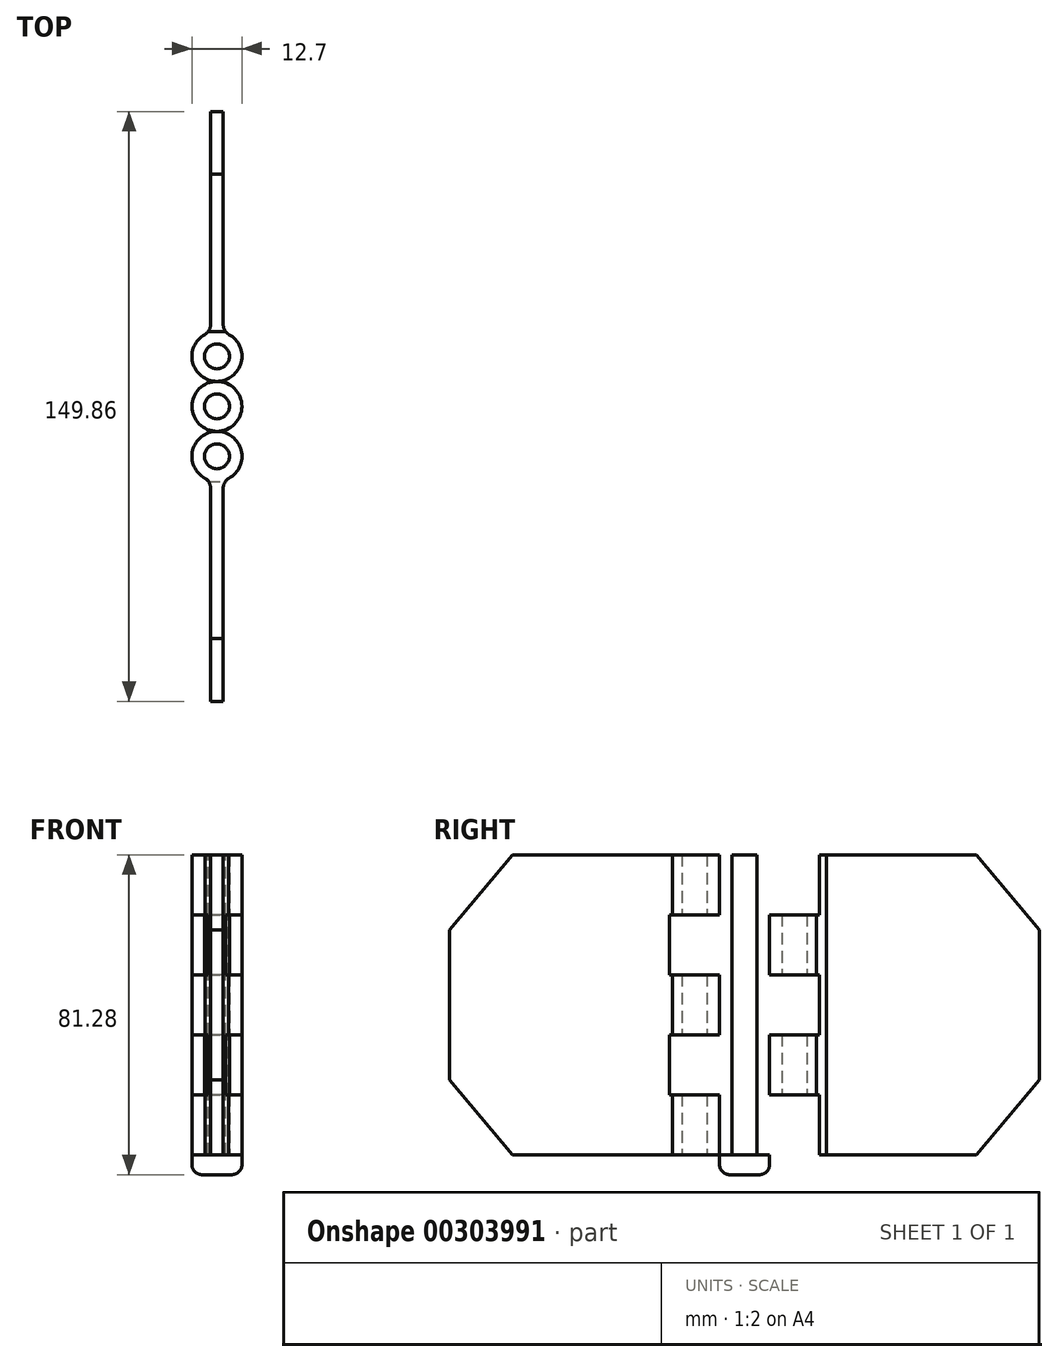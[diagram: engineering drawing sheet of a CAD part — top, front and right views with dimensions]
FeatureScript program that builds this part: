
annotation { "Feature Type Name" : "Feature", "Feature Type Description" : "" }
export const myFeature = defineFeature(function(context is Context, id is Id, definition is map)
    precondition{}
    {
        {
            var Q0;
            Q0=qCreatedBy(makeId("Right.planeOp"),FACE);
            var sketch = newSketch(context, id + "F0", { "sketchPlane" : qUnion([Q0])});
            skLineSegment(sketch, "E0.top", {"start": v(0, 76.2) * mm, "end": v(-39.9, 76.2) * mm});
            skLineSegment(sketch, "E0.left", {"start": v(0, 0) * mm, "end": v(0, 76.2) * mm});
            skLineSegment(sketch, "E1", {"start": v(-39.9, 76.2) * mm, "end": v(-55.88, 57.15) * mm});
            skLineSegment(sketch, "E2", {"start": v(-55.88, 19.05) * mm, "end": v(-39.9, 0) * mm});
            skLineSegment(sketch, "E3", {"start": v(-55.88, 57.15) * mm, "end": v(-55.88, 19.05) * mm});
            skLineSegment(sketch, "E4", {"start": v(-39.9, 0) * mm, "end": v(0, 0) * mm});
            skSolve(sketch);
        }
        {
            var Q0;
            Q0 = qSketchRegion(id + "F0", true);
            extrude(context, id + "F1", {"entities" : qUnion([Q0]), "depth" : 3.17 * mm});
        }
        {
            var Q0;
            Q0=makeQuery(id+"F1.opExtrude","SWEPT_FACE",FACE,{"disambiguationData":[OSD([sQuery(id+"F0.wireOp",EDGE,"E0.top")])]});
            var sketch = newSketch(context, id + "F2", { "sketchPlane" : qUnion([Q0])});
            skPoint(sketch, "E5", {"position": v(1.59, 6.35) * mm});
            skArc(sketch, "E6", {"start": v(4.6, 0.76) * mm, "mid": v(1.59, 12.7) * mm, "end": v(-1.43, 0.76) * mm});
            skArc(sketch, "E7", {"start": v(4.6, 0.76) * mm, "mid": v(3.56, -0.34) * mm, "end": v(3.18, -1.82) * mm});
            skArc(sketch, "E8", {"start": v(0, -1.82) * mm, "mid": v(-0.38, -0.34) * mm, "end": v(-1.43, 0.76) * mm});
            skLineSegment(sketch, "E9", {"start": v(0, -1.82) * mm, "end": v(0, 0) * mm});
            skLineSegment(sketch, "E10", {"start": v(0, 0) * mm, "end": v(3.18, 0) * mm});
            skLineSegment(sketch, "E11", {"start": v(3.18, 0) * mm, "end": v(3.18, -1.82) * mm});
            skPoint(sketch, "E12", {"position": v(1.59, 0) * mm});
            skSolve(sketch);
        }
        {
            var Q0;
            Q0 = qSketchRegion(id + "F2", true);
            var Q1;
            Q1=sQuery(id+"F2.wireOp",EDGE,"E6");
            extrude(context, id + "F3", {"entities" : qUnion([Q0]), "operationType" : NewBodyOperationType.ADD, "surfaceEntities" : qUnion([Q1]), "oppositeDirection" : true, "depth" : 76.2 * mm});
        }
        {
            var Q0;
            Q0=makeQuery(id+"F3.opExtrude","CAP_FACE",FACE,{"disambiguationData":[OSD([sQuery(id+"F2.wireOp",EDGE,"E6")])],"isStart":true});
            var sketch = newSketch(context, id + "F4", { "sketchPlane" : qUnion([Q0])});
            skPoint(sketch, "E13", {"position": v(1.59, 6.35) * mm});
            skCircle(sketch, "E14", {"center": v(1.59, 6.35) * mm, "radius": 3.18 * mm});
            skSolve(sketch);
        }
        {
            var Q0;
            Q0=sQuery(id+"F4.wireOp",VERTEX,"E13");
            var Q1;
            Q1=makeQuery(id+"F3.opExtrude","SWEPT_BODY",BODY,{"disambiguationData":[OSD([sQuery(id+"F2.wireOp",EDGE,"E6")])]});
            var Q2;
            Q2=makeQuery(id+"F1.opExtrude","SWEPT_BODY",BODY,{"disambiguationData":[OSD([sQuery(id+"F0.wireOp",EDGE,"E0.top"),sQuery(id+"F0.wireOp",EDGE,"E0.left"),sQuery(id+"F0.wireOp",EDGE,"E1"),sQuery(id+"F0.wireOp",EDGE,"E2"),sQuery(id+"F0.wireOp",EDGE,"E3"),sQuery(id+"F0.wireOp",EDGE,"E4")])]});
            hole(context, id + "F5", {"style" : HoleStyle.SIMPLE, "endStyle" : HoleEndStyle.THROUGH, "holeDiameter" : 6.35 * mm, "tappedDepth" : 12.7 * mm, "tapClearance" : 3, "locations" : qUnion([Q0]), "scope" : qUnion([Q1, Q2])});
        }
        {
            var Q0;
            Q0=qCreatedBy(makeId("Right.planeOp"),FACE);
            cPlane(context, id + "F6", {"entities" : qUnion([Q0]), "cplaneType" : CPlaneType.OFFSET, "offset" : 12.7 * mm, "width" : 152.4 * mm, "height" : 152.4 * mm});
        }
        {
            var Q0;
            Q0=qCreatedBy(id+"F6.planeOp",FACE);
            var sketch = newSketch(context, id + "F7", { "sketchPlane" : qUnion([Q0])});
            skLineSegment(sketch, "E15.bottom", {"start": v(12.7, 15.24) * mm, "end": v(0, 15.24) * mm});
            skLineSegment(sketch, "E15.top", {"start": v(12.7, 30.48) * mm, "end": v(0, 30.48) * mm});
            skLineSegment(sketch, "E15.left", {"start": v(12.7, 15.24) * mm, "end": v(12.7, 30.48) * mm});
            skLineSegment(sketch, "E15.right", {"start": v(0, 15.24) * mm, "end": v(0, 30.48) * mm});
            skLineSegment(sketch, "E16.bottom", {"start": v(12.7, 45.72) * mm, "end": v(0, 45.72) * mm});
            skLineSegment(sketch, "E16.top", {"start": v(12.7, 60.96) * mm, "end": v(0, 60.96) * mm});
            skLineSegment(sketch, "E16.left", {"start": v(12.7, 45.72) * mm, "end": v(12.7, 60.96) * mm});
            skLineSegment(sketch, "E16.right", {"start": v(0, 45.72) * mm, "end": v(0, 60.96) * mm});
            skSolve(sketch);
        }
        {
            var Q0;
            Q0 = qSketchRegion(id + "F7", true);
            extrude(context, id + "F8", {"entities" : qUnion([Q0]), "operationType" : NewBodyOperationType.REMOVE, "oppositeDirection" : true, "depth" : 19.05 * mm});
        }
        {
            var Q0;
            Q0=qCreatedBy(makeId("Right.planeOp"),FACE);
            var sketch = newSketch(context, id + "F9", { "sketchPlane" : qUnion([Q0])});
            skLineSegment(sketch, "E17.top", {"start": v(78, 76.2) * mm, "end": v(38.1, 76.2) * mm});
            skLineSegment(sketch, "E17.left", {"start": v(38.1, 0) * mm, "end": v(38.1, 76.2) * mm});
            skLineSegment(sketch, "E18", {"start": v(93.98, 57.15) * mm, "end": v(93.98, 19.05) * mm});
            skLineSegment(sketch, "E19", {"start": v(38.1, 0) * mm, "end": v(78, 0) * mm});
            skLineSegment(sketch, "E20", {"start": v(78, 76.2) * mm, "end": v(93.98, 57.15) * mm});
            skLineSegment(sketch, "E21", {"start": v(93.98, 19.05) * mm, "end": v(78, 0) * mm});
            skSolve(sketch);
        }
        {
            var Q0;
            Q0 = qSketchRegion(id + "F9", true);
            extrude(context, id + "F10", {"entities" : qUnion([Q0]), "depth" : 3.17 * mm});
        }
        {
            var Q0;
            Q0=makeQuery(id+"F10.opExtrude","SWEPT_FACE",FACE,{"disambiguationData":[OSD([sQuery(id+"F9.wireOp",EDGE,"E17.top")])]});
            var sketch = newSketch(context, id + "F11", { "sketchPlane" : qUnion([Q0])});
            skPoint(sketch, "E22", {"position": v(1.59, 38.1) * mm});
            skPoint(sketch, "E23", {"position": v(1.59, 31.75) * mm});
            skArc(sketch, "E24", {"start": v(-1.43, 37.34) * mm, "mid": v(1.59, 25.4) * mm, "end": v(4.6, 37.34) * mm});
            skArc(sketch, "E25", {"start": v(-1.43, 37.34) * mm, "mid": v(-0.4, 38.43) * mm, "end": v(0, 39.88) * mm});
            skArc(sketch, "E26", {"start": v(3.18, 39.88) * mm, "mid": v(3.57, 38.43) * mm, "end": v(4.6, 37.34) * mm});
            skLineSegment(sketch, "E27", {"start": v(0, 39.88) * mm, "end": v(0, 38.1) * mm});
            skLineSegment(sketch, "E28", {"start": v(0, 38.1) * mm, "end": v(3.18, 38.1) * mm});
            skLineSegment(sketch, "E29", {"start": v(3.18, 38.1) * mm, "end": v(3.18, 39.88) * mm});
            skSolve(sketch);
        }
        {
            var Q0;
            Q0 = qSketchRegion(id + "F11", true);
            extrude(context, id + "F12", {"entities" : qUnion([Q0]), "operationType" : NewBodyOperationType.ADD, "oppositeDirection" : true, "depth" : 76.2 * mm});
        }
        {
            var Q0;
            Q0=makeQuery(id+"F12.boolean.opBoolean","MERGE",FACE,{"derivedFrom":[makeQuery(id+"F10.opExtrude","SWEPT_FACE",FACE,{"disambiguationData":[OSD([sQuery(id+"F9.wireOp",EDGE,"E17.top")])]}),makeQuery(id+"F12.opExtrude","CAP_FACE",FACE,{"disambiguationData":[OSD([sQuery(id+"F11.wireOp",EDGE,"E24"),sQuery(id+"F11.wireOp",EDGE,"E25"),sQuery(id+"F11.wireOp",EDGE,"E26"),sQuery(id+"F11.wireOp",EDGE,"E27"),sQuery(id+"F11.wireOp",EDGE,"E28"),sQuery(id+"F11.wireOp",EDGE,"E29")])],"isStart":true})]});
            var sketch = newSketch(context, id + "F13", { "sketchPlane" : qUnion([Q0])});
            skCircle(sketch, "E30", {"center": v(1.59, 31.75) * mm, "radius": 3.18 * mm});
            skSolve(sketch);
        }
        {
            var Q0;
            Q0=sQuery(id+"F13.wireOp",VERTEX,"E30.center");
            var Q1;
            Q1=makeQuery(id+"F10.opExtrude","SWEPT_BODY",BODY,{"disambiguationData":[OSD([sQuery(id+"F9.wireOp",EDGE,"E17.top"),sQuery(id+"F9.wireOp",EDGE,"E17.left"),sQuery(id+"F9.wireOp",EDGE,"E18"),sQuery(id+"F9.wireOp",EDGE,"E19"),sQuery(id+"F9.wireOp",EDGE,"E20"),sQuery(id+"F9.wireOp",EDGE,"E21")])]});
            hole(context, id + "F14", {"style" : HoleStyle.SIMPLE, "endStyle" : HoleEndStyle.THROUGH, "holeDiameter" : 6.35 * mm, "tappedDepth" : 12.7 * mm, "tapClearance" : 3, "locations" : qUnion([Q0]), "scope" : qUnion([Q1])});
        }
        {
            var Q0;
            Q0=qCreatedBy(id+"F6.planeOp",FACE);
            var sketch = newSketch(context, id + "F15", { "sketchPlane" : qUnion([Q0])});
            skLineSegment(sketch, "E31.bottom", {"start": v(25.4, 76.2) * mm, "end": v(38.1, 76.2) * mm});
            skLineSegment(sketch, "E31.top", {"start": v(25.4, 60.96) * mm, "end": v(38.1, 60.96) * mm});
            skLineSegment(sketch, "E31.left", {"start": v(25.4, 76.2) * mm, "end": v(25.4, 60.96) * mm});
            skLineSegment(sketch, "E31.right", {"start": v(38.1, 76.2) * mm, "end": v(38.1, 60.96) * mm});
            skLineSegment(sketch, "E32.bottom", {"start": v(25.4, 45.72) * mm, "end": v(38.1, 45.72) * mm});
            skLineSegment(sketch, "E32.top", {"start": v(25.4, 30.48) * mm, "end": v(38.1, 30.48) * mm});
            skLineSegment(sketch, "E32.left", {"start": v(25.4, 45.72) * mm, "end": v(25.4, 30.48) * mm});
            skLineSegment(sketch, "E32.right", {"start": v(38.1, 45.72) * mm, "end": v(38.1, 30.48) * mm});
            skLineSegment(sketch, "E33.bottom", {"start": v(25.4, 15.24) * mm, "end": v(38.1, 15.24) * mm});
            skLineSegment(sketch, "E33.top", {"start": v(25.4, 0) * mm, "end": v(38.1, 0) * mm});
            skLineSegment(sketch, "E33.left", {"start": v(25.4, 15.24) * mm, "end": v(25.4, 0) * mm});
            skLineSegment(sketch, "E33.right", {"start": v(38.1, 15.24) * mm, "end": v(38.1, 0) * mm});
            skSolve(sketch);
        }
        {
            var Q0;
            Q0 = qSketchRegion(id + "F15", true);
            extrude(context, id + "F16", {"entities" : qUnion([Q0]), "operationType" : NewBodyOperationType.REMOVE, "oppositeDirection" : true, "depth" : 19.05 * mm});
        }
        {
            var Q0;
            Q0=qCreatedBy(makeId("Top.planeOp"),FACE);
            var sketch = newSketch(context, id + "F17", { "sketchPlane" : qUnion([Q0])});
            skPoint(sketch, "E34", {"position": v(1.59, 19.05) * mm});
            skCircle(sketch, "E35", {"center": v(1.59, 19.05) * mm, "radius": 3.18 * mm});
            skSolve(sketch);
        }
        {
            var Q0;
            Q0 = qSketchRegion(id + "F17", true);
            extrude(context, id + "F18", {"entities" : qUnion([Q0]), "depth" : 76.2 * mm});
        }
        {
            var Q0;
            Q0=makeQuery(id+"F18.opExtrude","CAP_FACE",FACE,{"disambiguationData":[OSD([sQuery(id+"F17.wireOp",EDGE,"E35")])],"isStart":true});
            var sketch = newSketch(context, id + "F19", { "sketchPlane" : qUnion([Q0])});
            skCircle(sketch, "E36", {"center": v(1.59, -19.05) * mm, "radius": 6.35 * mm});
            skSolve(sketch);
        }
        {
            var Q0;
            Q0 = qSketchRegion(id + "F19", true);
            extrude(context, id + "F20", {"entities" : qUnion([Q0]), "operationType" : NewBodyOperationType.ADD, "depth" : 5.08 * mm});
        }
        {
            var Q0;
            Q0=makeQuery(id+"F20.opExtrude","CAP_EDGE",EDGE,{"disambiguationData":[OSD([sQuery(id+"F19.wireOp",EDGE,"E36")])],"isStart":false});
            fillet(context, id + "F21", {"entities" : qUnion([Q0]), "radius" : 2.54 * mm, "tangentPropagation" : true, "allowEdgeOverflow" : false});
        }
    });
